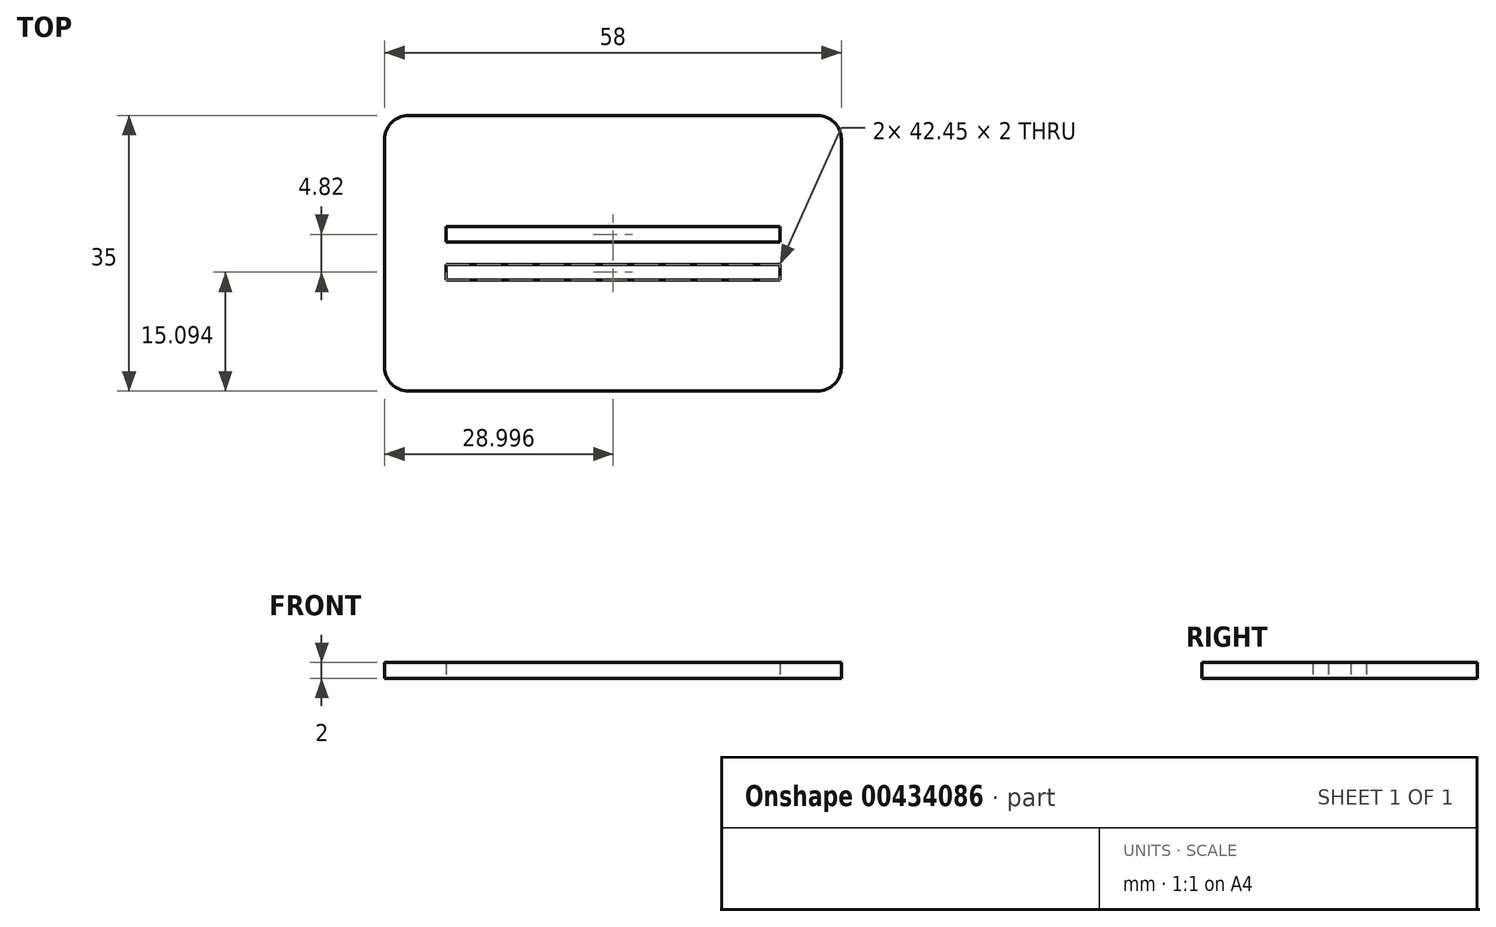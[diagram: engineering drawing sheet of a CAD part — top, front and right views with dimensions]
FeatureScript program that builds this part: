
annotation { "Feature Type Name" : "Feature", "Feature Type Description" : "" }
export const myFeature = defineFeature(function(context is Context, id is Id, definition is map)
    precondition{}
    {
        {
            var Q0;
            Q0=qCreatedBy(makeId("Top.planeOp"),FACE);
            var sketch = newSketch(context, id + "F0", { "sketchPlane" : qUnion([Q0])});
            skLineSegment(sketch, "E0.bottom", {"start": v(-65.71, 51.56) * mm, "end": v(-7.71, 51.56) * mm});
            skLineSegment(sketch, "E0.top", {"start": v(-65.71, 16.56) * mm, "end": v(-7.71, 16.56) * mm});
            skLineSegment(sketch, "E0.left", {"start": v(-65.71, 51.56) * mm, "end": v(-65.71, 16.56) * mm});
            skLineSegment(sketch, "E0.right", {"start": v(-7.71, 51.56) * mm, "end": v(-7.71, 16.56) * mm});
            skLineSegment(sketch, "E1", {"start": v(-81.04, 34.06) * mm, "end": v(-57.94, 34.06) * mm, "construction": true});
            skPoint(sketch, "E1.startSnap0", {"position": v(-65.71, 34.06) * mm});
            skLineSegment(sketch, "E2", {"start": v(-36.71, 62.88) * mm, "end": v(-36.71, 8.4) * mm, "construction": true});
            skPoint(sketch, "E2.startSnap0", {"position": v(-36.71, 51.56) * mm});
            skLineSegment(sketch, "E3.0", {"start": v(-81.04, 32.65) * mm, "end": v(7.2, 32.65) * mm, "construction": true});
            skLineSegment(sketch, "E4.0", {"start": v(-81.04, 35.47) * mm, "end": v(7.2, 35.47) * mm, "construction": true});
            skLineSegment(sketch, "E5", {"start": v(-57.94, 41.1) * mm, "end": v(-57.94, 35.47) * mm, "construction": true});
            skLineSegment(sketch, "E6.MirrorCS", {"start": v(-15.49, 41.1) * mm, "end": v(-15.49, 25.23) * mm, "construction": true});
            skLineSegment(sketch, "E7.bottom", {"start": v(-57.94, 35.47) * mm, "end": v(-15.49, 35.47) * mm, "construction": true});
            skLineSegment(sketch, "E7.top", {"start": v(-57.94, 37.47) * mm, "end": v(-15.49, 37.47) * mm, "construction": true});
            skLineSegment(sketch, "E7.left", {"start": v(-57.94, 35.47) * mm, "end": v(-57.94, 37.47) * mm, "construction": true});
            skLineSegment(sketch, "E7.right", {"start": v(-15.49, 35.47) * mm, "end": v(-15.49, 37.47) * mm, "construction": true});
            skLineSegment(sketch, "E8.top", {"start": v(-57.94, 32.65) * mm, "end": v(-15.49, 32.65) * mm});
            skLineSegment(sketch, "E8.right", {"start": v(-15.49, 34.06) * mm, "end": v(-15.49, 32.65) * mm});
            skLineSegment(sketch, "E9.bottom", {"start": v(-57.94, 37.47) * mm, "end": v(-15.49, 37.47) * mm});
            skLineSegment(sketch, "E9.top", {"start": v(-57.94, 35.47) * mm, "end": v(-15.49, 35.47) * mm});
            skLineSegment(sketch, "E9.left", {"start": v(-57.94, 37.47) * mm, "end": v(-57.94, 35.47) * mm});
            skLineSegment(sketch, "E9.right", {"start": v(-15.49, 37.47) * mm, "end": v(-15.49, 35.47) * mm});
            skLineSegment(sketch, "E10.trimOffspring", {"start": v(-15.49, 34.06) * mm, "end": v(7.2, 34.06) * mm, "construction": true});
            skLineSegment(sketch, "E11.trimOffspring", {"start": v(-57.94, 32.65) * mm, "end": v(-57.94, 25.23) * mm, "construction": true});
            skLineSegment(sketch, "E12.top", {"start": v(-57.94, 30.65) * mm, "end": v(-15.49, 30.65) * mm});
            skLineSegment(sketch, "E12.left", {"start": v(-57.94, 32.65) * mm, "end": v(-57.94, 30.65) * mm});
            skLineSegment(sketch, "E12.right", {"start": v(-15.49, 32.65) * mm, "end": v(-15.49, 30.65) * mm});
            skLineSegment(sketch, "E13", {"start": v(-57.94, 34.06) * mm, "end": v(-15.49, 34.06) * mm, "construction": true});
            skSolve(sketch);
        }
        {
            var Q0;
            Q0=makeQuery(id+"F0.imprint","IMPRINT",FACE,{"disambiguationData":[TD([[makeQuery(id+"F0.imprint","IMPRINT",EDGE,{"derivedFrom":sQuery(id+"F0.wireOp",EDGE,"E0.bottom")}),-1.0]])]});
            extrude(context, id + "F1", {"entities" : qUnion([Q0]), "depth" : 2 * mm, "offsetDistance" : 25 * mm});
        }
        {
            var Q0;
            Q0=makeQuery(id+"F1.opExtrude","SWEPT_EDGE",EDGE,{"disambiguationData":[OSD([sQuery(id+"F0.wireOp",EDGE,"E0.bottom"),sQuery(id+"F0.wireOp",EDGE,"E0.right")])]});
            var Q1;
            Q1=makeQuery(id+"F1.opExtrude","SWEPT_EDGE",EDGE,{"disambiguationData":[OSD([sQuery(id+"F0.wireOp",EDGE,"E0.top"),sQuery(id+"F0.wireOp",EDGE,"E0.left")])]});
            var Q2;
            Q2=makeQuery(id+"F1.opExtrude","SWEPT_EDGE",EDGE,{"disambiguationData":[OSD([sQuery(id+"F0.wireOp",EDGE,"E0.bottom"),sQuery(id+"F0.wireOp",EDGE,"E0.left")])]});
            var Q3;
            Q3=makeQuery(id+"F1.opExtrude","SWEPT_EDGE",EDGE,{"disambiguationData":[OSD([sQuery(id+"F0.wireOp",EDGE,"E0.top"),sQuery(id+"F0.wireOp",EDGE,"E0.right")])]});
            fillet(context, id + "F2", {"entities" : qUnion([Q0, Q1, Q2, Q3]), "radius" : 3 * mm, "tangentPropagation" : true, "allowEdgeOverflow" : false});
        }
    });
